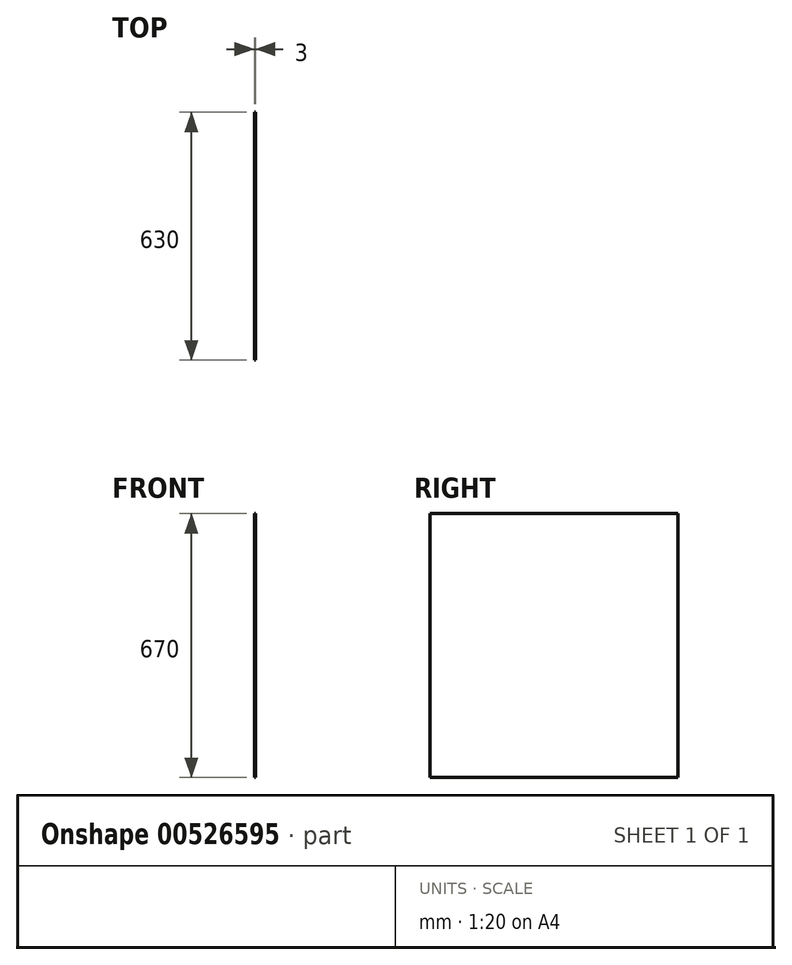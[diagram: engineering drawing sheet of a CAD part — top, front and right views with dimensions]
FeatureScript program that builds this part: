
annotation { "Feature Type Name" : "Feature", "Feature Type Description" : "" }
export const myFeature = defineFeature(function(context is Context, id is Id, definition is map)
    precondition{}
    {
        {
            var Q0;
            Q0=qCreatedBy(makeId("Right.planeOp"),FACE);
            var sketch = newSketch(context, id + "F0", { "sketchPlane" : qUnion([Q0])});
            skLineSegment(sketch, "E0.bottom", {"start": v(-315, -335) * mm, "end": v(315, -335) * mm});
            skLineSegment(sketch, "E0.top", {"start": v(-315, 335) * mm, "end": v(315, 335) * mm});
            skLineSegment(sketch, "E0.left", {"start": v(-315, -335) * mm, "end": v(-315, 335) * mm});
            skLineSegment(sketch, "E0.right", {"start": v(315, -335) * mm, "end": v(315, 335) * mm});
            skLineSegment(sketch, "E1", {"start": v(-667.2, -335) * mm, "end": v(-667.2, 335) * mm});
            skLineSegment(sketch, "E2", {"start": v(-677.2, 335) * mm, "end": v(-677.2, -335) * mm});
            skLineSegment(sketch, "E3", {"start": v(-677.2, 335) * mm, "end": v(-667.2, 335) * mm});
            skLineSegment(sketch, "E4.0.1.0", {"start": v(-677.2, 285) * mm, "end": v(-667.2, 285) * mm});
            skLineSegment(sketch, "E4.0.2.0", {"start": v(-677.2, 235) * mm, "end": v(-667.2, 235) * mm});
            skLineSegment(sketch, "E4.0.3.0", {"start": v(-677.2, 185) * mm, "end": v(-667.2, 185) * mm});
            skLineSegment(sketch, "E4.0.4.0", {"start": v(-677.2, 135) * mm, "end": v(-667.2, 135) * mm});
            skLineSegment(sketch, "E4.0.5.0", {"start": v(-677.2, 85) * mm, "end": v(-667.2, 85) * mm});
            skLineSegment(sketch, "E4.0.6.0", {"start": v(-677.2, 35) * mm, "end": v(-667.2, 35) * mm});
            skLineSegment(sketch, "E4.0.7.0", {"start": v(-677.2, -15) * mm, "end": v(-667.2, -15) * mm});
            skLineSegment(sketch, "E4.0.8.0", {"start": v(-677.2, -65) * mm, "end": v(-667.2, -65) * mm});
            skLineSegment(sketch, "E4.0.9.0", {"start": v(-677.2, -115) * mm, "end": v(-667.2, -115) * mm});
            skLineSegment(sketch, "E4.direction1", {"start": v(-677.2, 335) * mm, "end": v(-652.2, 335) * mm, "construction": true});
            skLineSegment(sketch, "E4.direction2", {"start": v(-677.2, 335) * mm, "end": v(-677.2, 285) * mm, "construction": true});
            skLineSegment(sketch, "E5.0.0.10", {"start": v(-677.2, -165) * mm, "end": v(-667.2, -165) * mm});
            skLineSegment(sketch, "E5.0.0.11", {"start": v(-677.2, -215) * mm, "end": v(-667.2, -215) * mm});
            skLineSegment(sketch, "E5.0.0.12", {"start": v(-677.2, -265) * mm, "end": v(-667.2, -265) * mm});
            skLineSegment(sketch, "E5.0.0.13", {"start": v(-677.2, -315) * mm, "end": v(-667.2, -315) * mm});
            skLineSegment(sketch, "E5.0.0.14", {"start": v(-677.2, -365) * mm, "end": v(-667.2, -365) * mm});
            skFitSpline(sketch, "E6", {"points": [v(-677.2, 335) * mm, v(-667.93, 285) * mm, v(-677.2, 235) * mm, v(-667.2, 185) * mm, v(-677.2, 135) * mm, v(-667.2, 85) * mm, v(-677.2, 35) * mm, v(-667.2, -15) * mm, v(-677.2, -65) * mm, v(-667.2, -115) * mm, v(-677.2, -165) * mm, v(-667.2, -215) * mm, v(-677.2, -265) * mm, v(-667.2, -315) * mm, v(-673.72, -335.16) * mm], "startDerivative": vector(220.65, -682.94) * mm, "endDerivative": vector(-217.68, -372.1) * mm});
            skSolve(sketch);
        }
        {
            var Q0;
            Q0=makeQuery(id+"F0.imprint","IMPRINT",FACE,{"disambiguationData":[TD([[makeQuery(id+"F0.imprint","IMPRINT",EDGE,{"derivedFrom":sQuery(id+"F0.wireOp",EDGE,"E0.bottom")}),1.0]])]});
            extrude(context, id + "F1", {"entities" : qUnion([Q0]), "depth" : 3 * mm, "offsetDistance" : 25 * mm});
        }
        {
            var Q0;
            Q0=sQuery(id+"F0.wireOp",EDGE,"E6");
            extrude(context, id + "F2", {"bodyType" : ExtendedToolBodyType.SURFACE, "surfaceEntities" : qUnion([Q0]), "depth" : 630 * mm, "offsetDistance" : 25 * mm});
        }
        {
            var Q0;
            Q0=makeQuery(id+"F0.imprint","IMPRINT",FACE,{"disambiguationData":[TD([[makeQuery(id+"F0.imprint","IMPRINT",EDGE,{"derivedFrom":sQuery(id+"F0.wireOp",EDGE,"E0.bottom")}),1.0]])]});
            var sketch = newSketch(context, id + "F3", { "sketchPlane" : qUnion([Q0])});
            skFitSpline(sketch, "E7", {"points": [v(-196.07, 42.95) * mm, v(-176.32, 49.4) * mm, v(-156.58, 40.68) * mm, v(-131.9, 48.27) * mm], "startDerivative": vector(62.74, 35.66) * mm, "endDerivative": vector(71.87, 38.04) * mm});
            skSolve(sketch);
        }
        {
            var Q0;
            Q0=sQuery(id+"F3.wireOp",EDGE,"E7");
            extrude(context, id + "F4", {"bodyType" : ExtendedToolBodyType.SURFACE, "surfaceEntities" : qUnion([Q0]), "depth" : 300 * mm, "offsetDistance" : 25 * mm});
        }
    });
